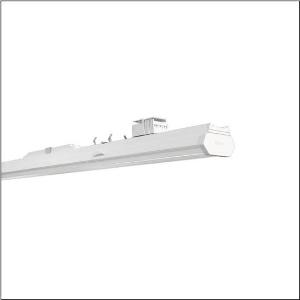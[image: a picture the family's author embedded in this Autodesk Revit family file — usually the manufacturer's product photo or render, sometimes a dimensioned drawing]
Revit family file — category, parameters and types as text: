
# Revit family: licross_11_protected_ho_51td12dn4fxm3s4
name_source: partatom
category: Lighting Fixtures
units: mm (PartAtom-declared; Revit-internal decimal feet)

## family parameters
Cut with Voids When Loaded = No
Host = Face
Light Source = No
Part Type = Normal
Room Calculation Point = No
Round Connector Dimension = Use Diameter
Shared = No

## types (1)
- --- (1 x LED, 970 lm, 7.4 W, 4000K)
    Apparent Load = 7 VA
    CIE Flux Codes = 70 91 97 98 100
    Color Rendering = 80
    Color Temperature = 4000K
    Default Elevation = 1800 mm
    Description = Licross 11 Protected HO, luminaire insert, of sheet steel, galvanised, coil coated, white, length: 1.500mm, width: 90mm, height: 101mm, LED rated luminous flux: 15.270lm, light colour: 840, SDCM (Standard Deviation of Colour Matching)MacAdam ≤ 2 SDCM (initial), control gear: DALI 2, with plug, 6-pole, with phase selection, for trunking rail, 9 or 11-core, mains connection: 220..240V, AC, 50/60Hz, rated input power: 91W, for trunking rail, 9-/11-core, internal wiring halogen-free, for emergency light function, converter,control gear: single battery element, battery: LiFePO4, 9Ah, primary light control with lens, of plastic, primary optical cover: cover, of PMMA, light emission: direct distribution, primary light characteristic: symmetric, protection rating (complete): IP54, insulation class (complete): insulation class I (protective earthing), certification: CE, UKCA, protection symbol: D if used in an environment with non-conductive dust loads with corresponding accessories, impact resistance: IK06, permissible ambient temperature for indoor applications: +5..+30°C, standard: EN 60598-2-22, LABS conformity tested according to VDMA 24364:2018-05, reducing of maximum allowable ambient temperature of 5°C with ceiling mounting, corresponds to IFS (International Featured Standards) requirements for safety and quality in the food industry, The light source and the operating device comply with the requirements of the Ecodesign Regulation (EU) 2019/2020 and are replaceable in accordance with this regulation, packaging unit: 1 piece
    Height = 92 mm
    Lamp = 1 x LED
    Lamp Light Flux = 970 lm
    Lamp Power = 7.4 W
    Lamp count = 1
    Length = 1500 mm
    Luminous efficacy = 131 lm/W
    Manufacturer = Siteco
    ModVariant = No
    Model = 51TD12DN4FXM3S4
    Mounting Place = Ceiling
    Mounting Type = Pendant
    Number of Poles = 1
    OnlyDefault = Yes
    Power Factor = 1
    Product Name = Licross 11 Protected HO
    Product group = luminaire insert | ceiling pendant
    ProductGroupID = 901
    Protection Class = Protection class I
    Protection Degree = IP 54
    RLX_Detail_Level = 1
    RLX_Emergency_Light_Flux = 0 lm
    RLX_Emergency_Type = 0
    RLX_Emergency_Type_DB = No
    RlxData = <blob elided: 25165 chars, md5=6f2b5250>
    Socket = socket
    Standby Power = 0 W
    System Light Flux = 970 lm
    System Power = 7 W
    Type Comments = : emergency light operation: 3 h
    Type Image = l_1256145.jpg
    URL = http://relux.com
    VarID = @adj_096257
    Voltage = 0 V
    Weight = 0.00 kg
    Width = 88 mm

## geometry (parser evidence)
native form markers: Blend x4, Sweep x11
no freeform markers — native parametric forms only
